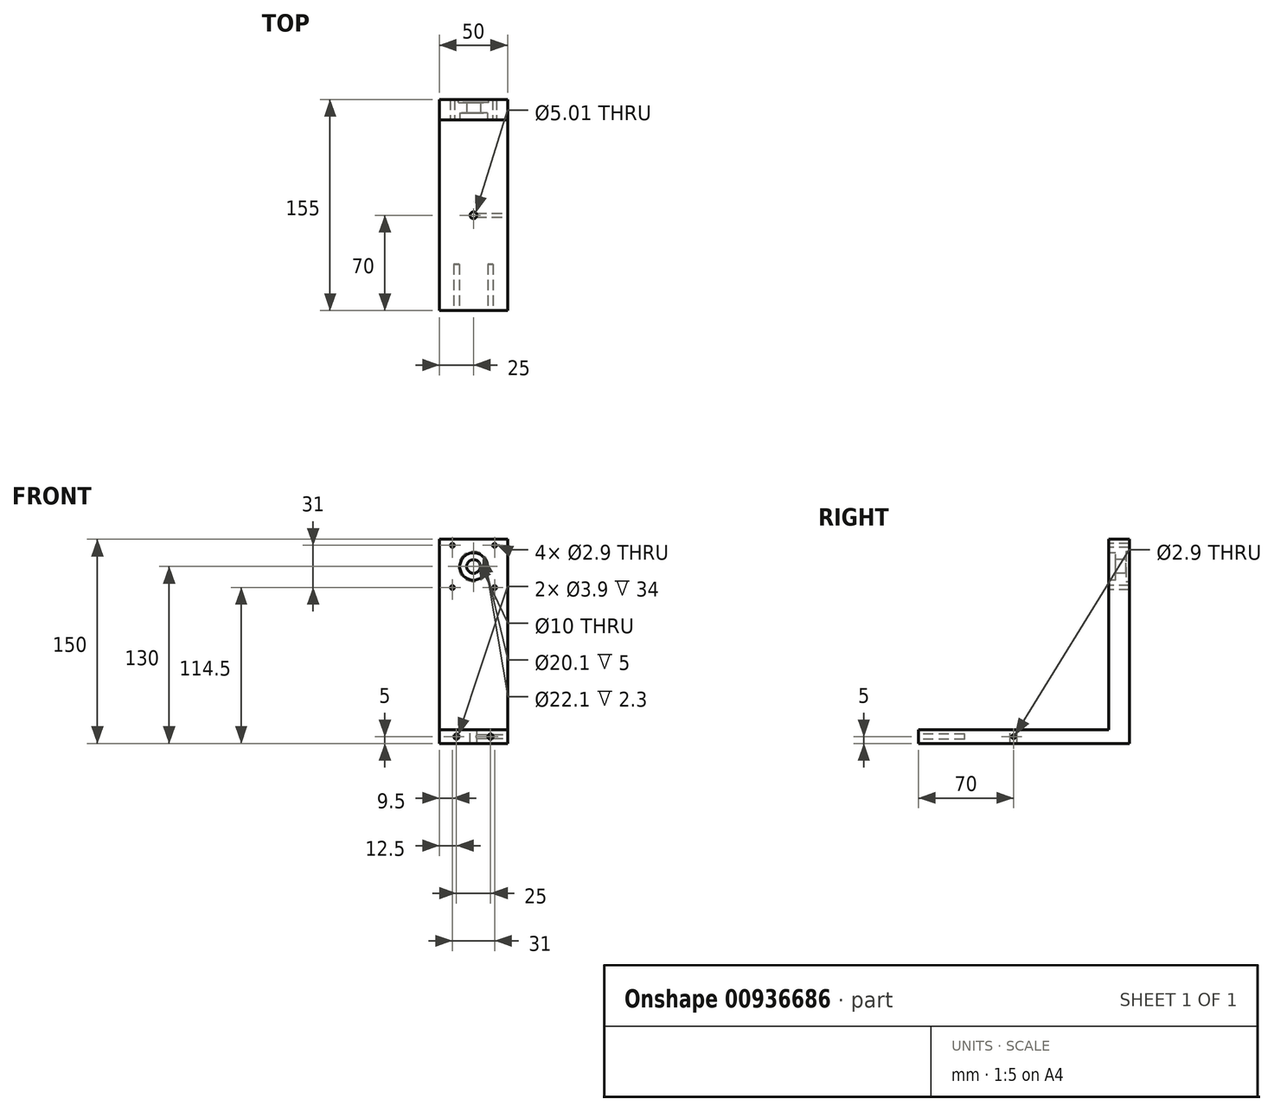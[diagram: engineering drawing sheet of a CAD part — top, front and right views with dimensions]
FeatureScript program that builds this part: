
annotation { "Feature Type Name" : "Feature", "Feature Type Description" : "" }
export const myFeature = defineFeature(function(context is Context, id is Id, definition is map)
    precondition{}
    {
        {
            var Q0;
            Q0=qCreatedBy(makeId("Right.planeOp"),FACE);
            var sketch = newSketch(context, id + "F0", { "sketchPlane" : qUnion([Q0])});
            skLineSegment(sketch, "E0.bottom", {"start": v(-15, 10) * mm, "end": v(-155, 10) * mm});
            skLineSegment(sketch, "E0.left", {"start": v(-15, 10) * mm, "end": v(-15, 150) * mm});
            skLineSegment(sketch, "E1.bottom", {"start": v(0, 0) * mm, "end": v(-155, 0) * mm});
            skLineSegment(sketch, "E1.top", {"start": v(0, 150) * mm, "end": v(-15, 150) * mm});
            skLineSegment(sketch, "E1.left", {"start": v(0, 0) * mm, "end": v(0, 150) * mm});
            skLineSegment(sketch, "E1.right", {"start": v(-155, 0) * mm, "end": v(-155, 10) * mm});
            skSolve(sketch);
        }
        {
            var Q0;
            Q0=makeQuery(id+"F0.imprint","IMPRINT",FACE,{"disambiguationData":[TD([[makeQuery(id+"F0.imprint","IMPRINT",EDGE,{"derivedFrom":sQuery(id+"F0.wireOp",EDGE,"E0.bottom")}),1.0]])]});
            extrude(context, id + "F1", {"entities" : qUnion([Q0]), "depth" : 50 * mm, "offsetDistance" : 25 * mm});
        }
        {
            var Q0;
            Q0=makeQuery(id+"F1.opExtrude","SWEPT_FACE",FACE,{"disambiguationData":[OSD([sQuery(id+"F0.wireOp",EDGE,"E0.left")])]});
            var sketch = newSketch(context, id + "F2", { "sketchPlane" : qUnion([Q0])});
            skCircle(sketch, "E2", {"center": v(25, 130) * mm, "radius": 5 * mm});
            skCircle(sketch, "E3", {"center": v(25, 130) * mm, "radius": 10.05 * mm});
            skCircle(sketch, "E4", {"center": v(9.5, 114.5) * mm, "radius": 1.45 * mm});
            skCircle(sketch, "E5", {"center": v(40.5, 114.5) * mm, "radius": 1.45 * mm});
            skCircle(sketch, "E6", {"center": v(40.5, 145.5) * mm, "radius": 1.45 * mm});
            skCircle(sketch, "E7", {"center": v(9.5, 145.5) * mm, "radius": 1.45 * mm});
            skSolve(sketch);
        }
        {
            var Q0;
            Q0=makeQuery(id+"F2.imprint","IMPRINT",FACE,{"disambiguationData":[TD([[makeQuery(id+"F2.imprint","IMPRINT",EDGE,{"derivedFrom":sQuery(id+"F2.wireOp",EDGE,"E2")}),1.0]])]});
            var Q1;
            Q1=makeQuery(id+"F2.imprint","IMPRINT",FACE,{"disambiguationData":[TD([[makeQuery(id+"F2.imprint","IMPRINT",EDGE,{"derivedFrom":sQuery(id+"F2.wireOp",EDGE,"E7")}),1.0]])]});
            var Q2;
            Q2=makeQuery(id+"F2.imprint","IMPRINT",FACE,{"disambiguationData":[TD([[makeQuery(id+"F2.imprint","IMPRINT",EDGE,{"derivedFrom":sQuery(id+"F2.wireOp",EDGE,"E4")}),1.0]])]});
            var Q3;
            Q3=makeQuery(id+"F2.imprint","IMPRINT",FACE,{"disambiguationData":[TD([[makeQuery(id+"F2.imprint","IMPRINT",EDGE,{"derivedFrom":sQuery(id+"F2.wireOp",EDGE,"E5")}),1.0]])]});
            var Q4;
            Q4=makeQuery(id+"F2.imprint","IMPRINT",FACE,{"disambiguationData":[TD([[makeQuery(id+"F2.imprint","IMPRINT",EDGE,{"derivedFrom":sQuery(id+"F2.wireOp",EDGE,"E6")}),1.0]])]});
            extrude(context, id + "F3", {"entities" : qUnion([Q0, Q1, Q2, Q3, Q4]), "operationType" : NewBodyOperationType.REMOVE, "endBound" : BoundingType.UP_TO_NEXT, "oppositeDirection" : true, "depth" : 25 * mm, "offsetDistance" : 25 * mm});
        }
        {
            var Q0;
            Q0=makeQuery(id+"F2.imprint","IMPRINT",FACE,{"disambiguationData":[TD([[makeQuery(id+"F2.imprint","IMPRINT",EDGE,{"derivedFrom":sQuery(id+"F2.wireOp",EDGE,"E2")}),-1.0]])]});
            extrude(context, id + "F4", {"entities" : qUnion([Q0]), "operationType" : NewBodyOperationType.REMOVE, "oppositeDirection" : true, "depth" : 5 * mm, "offsetDistance" : 25 * mm});
        }
        {
            var Q0;
            Q0=makeQuery(id+"F1.opExtrude","SWEPT_FACE",FACE,{"disambiguationData":[OSD([sQuery(id+"F0.wireOp",EDGE,"E1.left")])]});
            var sketch = newSketch(context, id + "F5", { "sketchPlane" : qUnion([Q0])});
            skCircle(sketch, "E8", {"center": v(-25, 130) * mm, "radius": 11.05 * mm});
            skSolve(sketch);
        }
        {
            var Q0;
            Q0=makeQuery(id+"F5.imprint","IMPRINT",FACE,{"disambiguationData":[TD([[makeQuery(id+"F5.imprint","IMPRINT",EDGE,{"derivedFrom":sQuery(id+"F5.wireOp",EDGE,"E8")}),1.0]])]});
            extrude(context, id + "F6", {"entities" : qUnion([Q0]), "operationType" : NewBodyOperationType.REMOVE, "oppositeDirection" : true, "depth" : 2.3 * mm, "offsetDistance" : 25 * mm});
        }
        {
            var Q0;
            Q0=makeQuery(id+"F1.opExtrude","SWEPT_FACE",FACE,{"disambiguationData":[OSD([sQuery(id+"F0.wireOp",EDGE,"E1.right")])]});
            var sketch = newSketch(context, id + "F7", { "sketchPlane" : qUnion([Q0])});
            skCircle(sketch, "E9", {"center": v(12.5, 5) * mm, "radius": 1.95 * mm});
            skCircle(sketch, "E10", {"center": v(37.5, 5) * mm, "radius": 1.95 * mm});
            skSolve(sketch);
        }
        {
            var Q0;
            Q0=makeQuery(id+"F7.imprint","IMPRINT",FACE,{"disambiguationData":[TD([[makeQuery(id+"F7.imprint","IMPRINT",EDGE,{"derivedFrom":sQuery(id+"F7.wireOp",EDGE,"E9")}),1.0]])]});
            var Q1;
            Q1=makeQuery(id+"F7.imprint","IMPRINT",FACE,{"disambiguationData":[TD([[makeQuery(id+"F7.imprint","IMPRINT",EDGE,{"derivedFrom":sQuery(id+"F7.wireOp",EDGE,"E10")}),1.0]])]});
            extrude(context, id + "F8", {"entities" : qUnion([Q0, Q1]), "operationType" : NewBodyOperationType.REMOVE, "oppositeDirection" : true, "depth" : 34 * mm, "offsetDistance" : 25 * mm});
        }
        {
            var Q0;
            Q0=makeQuery(id+"F1.opExtrude","SWEPT_FACE",FACE,{"disambiguationData":[OSD([sQuery(id+"F0.wireOp",EDGE,"E0.bottom")])]});
            var sketch = newSketch(context, id + "F9", { "sketchPlane" : qUnion([Q0])});
            skCircle(sketch, "E11", {"center": v(25, -85) * mm, "radius": 2.5 * mm});
            skSolve(sketch);
        }
        {
            var Q0;
            Q0=makeQuery(id+"F9.imprint","IMPRINT",FACE,{"disambiguationData":[TD([[makeQuery(id+"F9.imprint","IMPRINT",EDGE,{"derivedFrom":sQuery(id+"F9.wireOp",EDGE,"E11")}),1.0]])]});
            extrude(context, id + "F10", {"entities" : qUnion([Q0]), "operationType" : NewBodyOperationType.REMOVE, "endBound" : BoundingType.UP_TO_NEXT, "oppositeDirection" : true, "depth" : 25 * mm, "offsetDistance" : 25 * mm});
        }
        {
            var Q0;
            Q0=makeQuery(id+"F1.opExtrude","CAP_FACE",FACE,{"disambiguationData":[OSD([sQuery(id+"F0.wireOp",EDGE,"E0.bottom"),sQuery(id+"F0.wireOp",EDGE,"E0.left"),sQuery(id+"F0.wireOp",EDGE,"E1.bottom"),sQuery(id+"F0.wireOp",EDGE,"E1.top"),sQuery(id+"F0.wireOp",EDGE,"E1.left"),sQuery(id+"F0.wireOp",EDGE,"E1.right")])],"isStart":false});
            var sketch = newSketch(context, id + "F11", { "sketchPlane" : qUnion([Q0])});
            skCircle(sketch, "E12", {"center": v(-85, 5) * mm, "radius": 1.45 * mm});
            skSolve(sketch);
        }
        {
            var Q0;
            Q0=makeQuery(id+"F11.imprint","IMPRINT",FACE,{"disambiguationData":[TD([[makeQuery(id+"F11.imprint","IMPRINT",EDGE,{"derivedFrom":sQuery(id+"F11.wireOp",EDGE,"E12")}),1.0]])]});
            extrude(context, id + "F12", {"entities" : qUnion([Q0]), "operationType" : NewBodyOperationType.REMOVE, "endBound" : BoundingType.UP_TO_NEXT, "oppositeDirection" : true, "depth" : 25 * mm, "offsetDistance" : 25 * mm});
        }
    });
